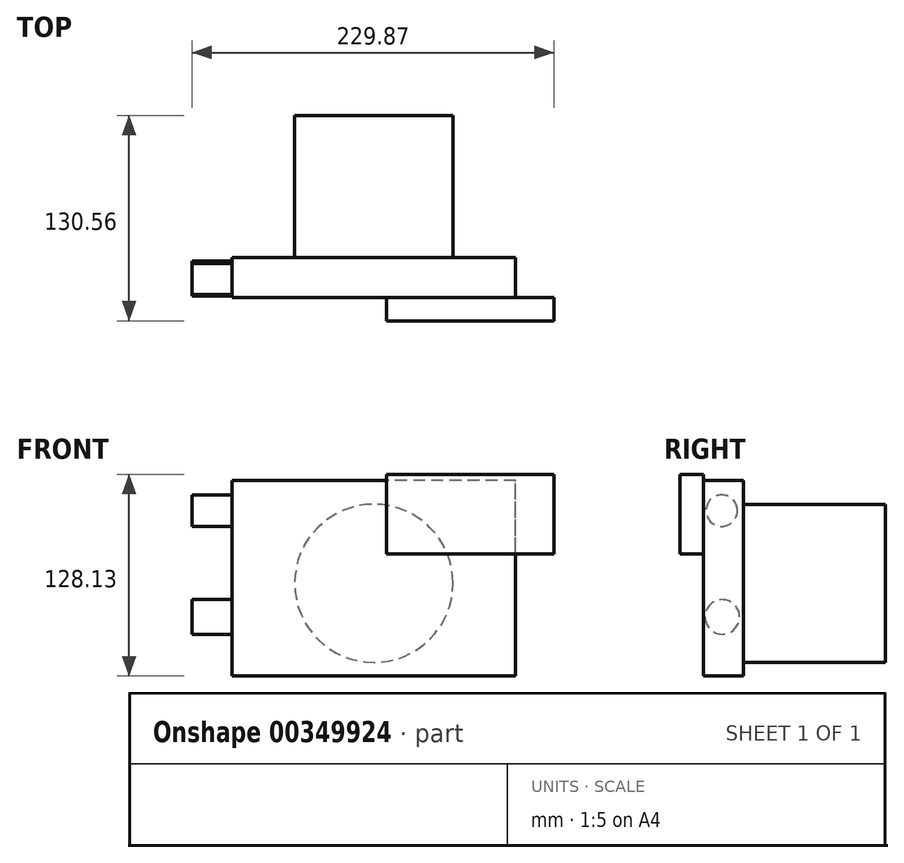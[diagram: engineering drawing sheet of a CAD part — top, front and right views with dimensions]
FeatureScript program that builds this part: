
annotation { "Feature Type Name" : "Feature", "Feature Type Description" : "" }
export const myFeature = defineFeature(function(context is Context, id is Id, definition is map)
    precondition{}
    {
        {
            var Q0;
            Q0=qCreatedBy(makeId("Front.planeOp"),FACE);
            var sketch = newSketch(context, id + "F0", { "sketchPlane" : qUnion([Q0])});
            skLineSegment(sketch, "E0.bottom", {"start": v(90.09, -62.11) * mm, "end": v(-90.09, -62.11) * mm});
            skLineSegment(sketch, "E0.top", {"start": v(90.09, 62.11) * mm, "end": v(-90.09, 62.11) * mm});
            skLineSegment(sketch, "E0.left", {"start": v(90.09, -62.11) * mm, "end": v(90.09, 62.11) * mm});
            skLineSegment(sketch, "E0.right", {"start": v(-90.09, -62.11) * mm, "end": v(-90.09, 62.11) * mm});
            skPoint(sketch, "E0.middle", {"position": v(0, 0) * mm});
            skSolve(sketch);
        }
        {
            var Q0;
            Q0 = qSketchRegion(id + "F0", true);
            extrude(context, id + "F1", {"entities" : qUnion([Q0]), "depth" : 25.4 * mm, "offsetDistance" : 25.4 * mm});
        }
        {
            var Q0;
            Q0=makeQuery(id+"F1.opExtrude","SWEPT_FACE",FACE,{"disambiguationData":[OSD([sQuery(id+"F0.wireOp",EDGE,"E0.right")])]});
            var sketch = newSketch(context, id + "F2", { "sketchPlane" : qUnion([Q0])});
            skCircle(sketch, "E1", {"center": v(13.8, 43) * mm, "radius": 9.96 * mm});
            skCircle(sketch, "E2", {"center": v(13.42, -24.5) * mm, "radius": 11 * mm});
            skSolve(sketch);
        }
        {
            var Q0;
            Q0 = qSketchRegion(id + "F2", true);
            extrude(context, id + "F3", {"entities" : qUnion([Q0]), "operationType" : NewBodyOperationType.ADD, "depth" : 25.4 * mm, "offsetDistance" : 25.4 * mm});
        }
        {
            var Q0;
            Q0=makeQuery(id+"F1.opExtrude","CAP_FACE",FACE,{"disambiguationData":[OSD([sQuery(id+"F0.wireOp",EDGE,"E0.bottom"),sQuery(id+"F0.wireOp",EDGE,"E0.top"),sQuery(id+"F0.wireOp",EDGE,"E0.left"),sQuery(id+"F0.wireOp",EDGE,"E0.right")])],"isStart":true});
            var sketch = newSketch(context, id + "F4", { "sketchPlane" : qUnion([Q0])});
            skCircle(sketch, "E3", {"center": v(0, -3.16) * mm, "radius": 50.24 * mm});
            skSolve(sketch);
        }
        {
            var Q0;
            Q0 = qSketchRegion(id + "F4", true);
            extrude(context, id + "F5", {"entities" : qUnion([Q0]), "operationType" : NewBodyOperationType.ADD, "depth" : 90.17 * mm, "offsetDistance" : 25.4 * mm});
        }
        {
            var Q0;
            Q0=makeQuery(id+"F1.opExtrude","CAP_FACE",FACE,{"disambiguationData":[OSD([sQuery(id+"F0.wireOp",EDGE,"E0.bottom"),sQuery(id+"F0.wireOp",EDGE,"E0.top"),sQuery(id+"F0.wireOp",EDGE,"E0.left"),sQuery(id+"F0.wireOp",EDGE,"E0.right")])],"isStart":false});
            var sketch = newSketch(context, id + "F6", { "sketchPlane" : qUnion([Q0])});
            skLineSegment(sketch, "E4.bottom", {"start": v(114.38, 15.5) * mm, "end": v(7.9, 15.5) * mm});
            skLineSegment(sketch, "E4.top", {"start": v(114.38, 66.02) * mm, "end": v(7.9, 66.02) * mm});
            skLineSegment(sketch, "E4.left", {"start": v(114.38, 15.5) * mm, "end": v(114.38, 66.02) * mm});
            skLineSegment(sketch, "E4.right", {"start": v(7.9, 15.5) * mm, "end": v(7.9, 66.02) * mm});
            skPoint(sketch, "E4.middle", {"position": v(61.14, 40.76) * mm});
            skSolve(sketch);
        }
        {
            var Q0;
            Q0 = qSketchRegion(id + "F6", true);
            extrude(context, id + "F7", {"entities" : qUnion([Q0]), "operationType" : NewBodyOperationType.ADD, "depth" : 15 * mm, "offsetDistance" : 25.4 * mm});
        }
    });
